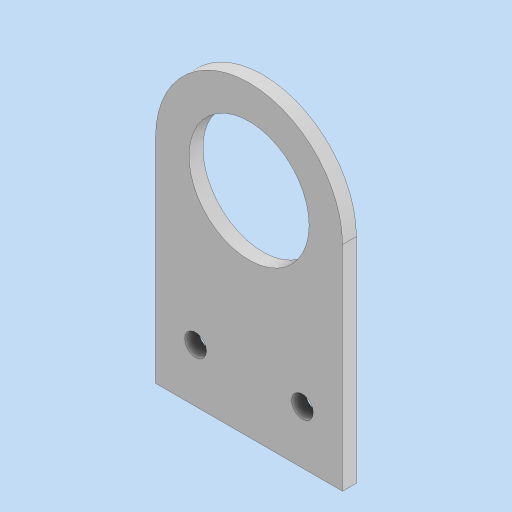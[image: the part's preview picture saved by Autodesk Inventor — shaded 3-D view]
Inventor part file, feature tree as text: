
AUTODESK INVENTOR PART (.ipt)
format: ipt  version: 2024 (Build 280153000, 153)  size: 111,616 bytes
history: native  units: in
note: dims shown in document units (in); Inventor stores cm internally (conversion verified against a paired STEP export)
features: extrude x1, sketch x1
ambient origin geometry x8: Origin, YZ Plane, XZ Plane, XY Plane, X Axis, Y Axis, Z Axis, Center Point
bodies: Solid1 (feature_tree)
feature tree (2):
  extrude  "Extrusion1"  Depth=0.13in
  sketch  "Sketch1"  dims[d0=1.75in d1=1.125in d8=0.13in d9=0.0in d10=0.203in d11=0.203in d12=0.5in d13=0.5in d14=0.5in d15=0.5in]
